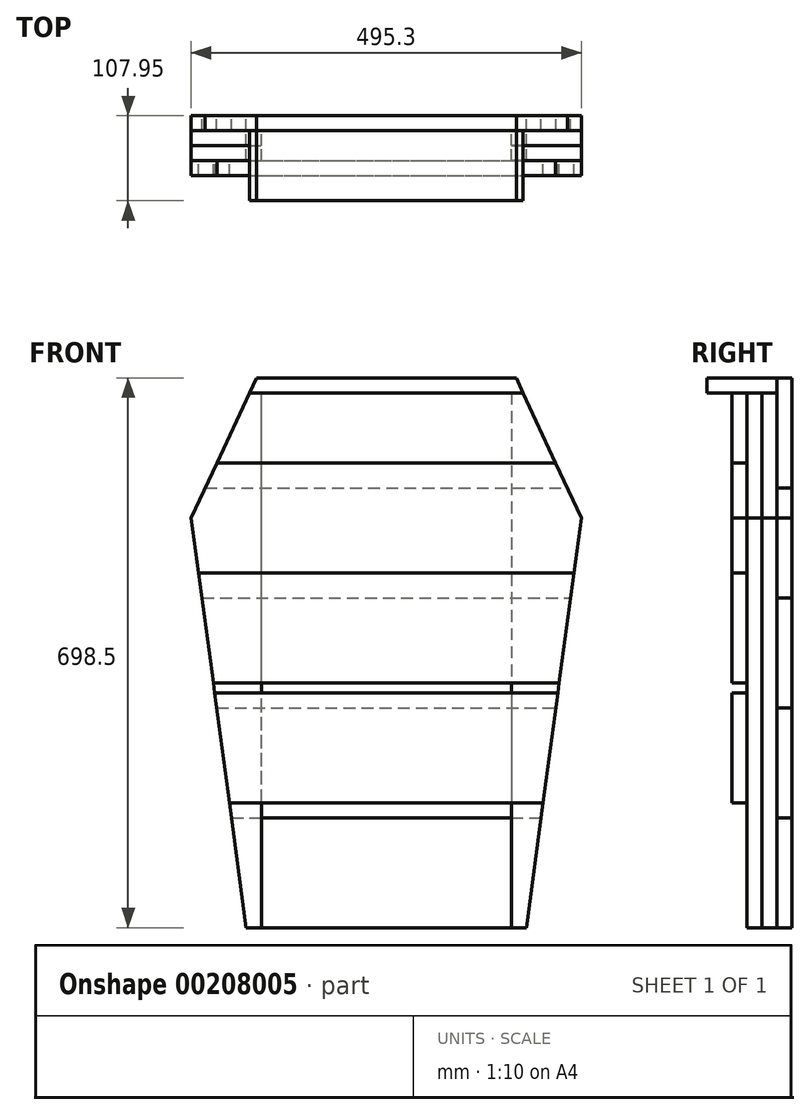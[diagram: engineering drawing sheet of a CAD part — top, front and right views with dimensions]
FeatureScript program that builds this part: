
annotation { "Feature Type Name" : "Feature", "Feature Type Description" : "" }
export const myFeature = defineFeature(function(context is Context, id is Id, definition is map)
    precondition{}
    {
        {
            var Q0;
            Q0=qCreatedBy(makeId("Front.planeOp"),FACE);
            var sketch = newSketch(context, id + "F0", { "sketchPlane" : qUnion([Q0])});
            skLineSegment(sketch, "E0", {"start": v(0, 0) * mm, "end": v(0, -698.5) * mm, "construction": true});
            skLineSegment(sketch, "E1", {"start": v(-165.1, 0) * mm, "end": v(165.1, 0) * mm});
            skLineSegment(sketch, "E2", {"start": v(165.1, 0) * mm, "end": v(247.65, -177.8) * mm});
            skLineSegment(sketch, "E3", {"start": v(247.65, -177.8) * mm, "end": v(177.8, -698.5) * mm});
            skLineSegment(sketch, "E4", {"start": v(177.8, -698.5) * mm, "end": v(-177.8, -698.5) * mm});
            skLineSegment(sketch, "E5", {"start": v(-177.8, -698.5) * mm, "end": v(-247.65, -177.8) * mm});
            skLineSegment(sketch, "E6", {"start": v(-247.65, -177.8) * mm, "end": v(-165.1, 0) * mm});
            skSolve(sketch);
        }
        {
            var Q0;
            Q0=qCreatedBy(makeId("Front.planeOp"),FACE);
            var sketch = newSketch(context, id + "F1", { "sketchPlane" : qUnion([Q0])});
            skLineSegment(sketch, "E7.0", {"start": v(-177.8, -698.5) * mm, "end": v(-247.65, -177.8) * mm});
            skLineSegment(sketch, "E8.0", {"start": v(-247.65, -177.8) * mm, "end": v(-165.1, 0) * mm});
            skLineSegment(sketch, "E8.1", {"start": v(-165.1, 0) * mm, "end": v(165.1, 0) * mm});
            skLineSegment(sketch, "E8.2", {"start": v(165.1, 0) * mm, "end": v(247.65, -177.8) * mm});
            skLineSegment(sketch, "E8.3", {"start": v(247.65, -177.8) * mm, "end": v(177.8, -698.5) * mm});
            skLineSegment(sketch, "E9", {"start": v(-229.96, -139.7) * mm, "end": v(229.96, -139.7) * mm});
            skLineSegment(sketch, "E10", {"start": v(-234.02, -279.4) * mm, "end": v(234.02, -279.4) * mm});
            skLineSegment(sketch, "E11", {"start": v(-215.28, -419.1) * mm, "end": v(215.28, -419.1) * mm});
            skLineSegment(sketch, "E12", {"start": v(-196.54, -558.8) * mm, "end": v(196.54, -558.8) * mm});
            skLineSegment(sketch, "E13", {"start": v(-177.8, -698.5) * mm, "end": v(177.8, -698.5) * mm});
            skSolve(sketch);
        }
        {
            var Q0;
            {var subQ0=sQuery(id+"F1.wireOp",EDGE,"E11");Q0=makeQuery(id+"F1.imprint","IMPRINT",FACE,{"disambiguationData":[TD([[makeQuery(id+"F1.imprint","IMPRINT",EDGE,{"derivedFrom":subQ0}),-1.0]])]});}
            var Q1;
            {var subQ7=sQuery(id+"F1.wireOp",EDGE,"E9");Q1=makeQuery(id+"F1.imprint","IMPRINT",FACE,{"disambiguationData":[TD([[makeQuery(id+"F1.imprint","IMPRINT",EDGE,{"derivedFrom":subQ7}),-1.0]])]});}
            extrude(context, id + "F2", {"entities" : qUnion([Q0, Q1]), "depth" : 19.05 * mm});
        }
        {
            var Q0;
            {var subQ0=sQuery(id+"F1.wireOp",EDGE,"E12");Q0=makeQuery(id+"F1.imprint","IMPRINT",FACE,{"disambiguationData":[TD([[makeQuery(id+"F1.imprint","IMPRINT",EDGE,{"derivedFrom":subQ0}),-1.0]])]});}
            var Q1;
            {var subQ0=sQuery(id+"F1.wireOp",EDGE,"E10");Q1=makeQuery(id+"F1.imprint","IMPRINT",FACE,{"disambiguationData":[TD([[makeQuery(id+"F1.imprint","IMPRINT",EDGE,{"derivedFrom":subQ0}),-1.0]])]});}
            var Q2;
            {var subQ0=sQuery(id+"F1.wireOp",EDGE,"E8.1");Q2=makeQuery(id+"F1.imprint","IMPRINT",FACE,{"disambiguationData":[TD([[makeQuery(id+"F1.imprint","IMPRINT",EDGE,{"derivedFrom":subQ0}),-1.0]])]});}
            extrude(context, id + "F3", {"entities" : qUnion([Q0, Q1, Q2]), "depth" : 19.05 * mm});
        }
        {
            var Q0;
            Q0=makeQuery(id+"F3.opExtrude","CAP_FACE",FACE,{"disambiguationData":[OSD([sQuery(id+"F1.wireOp",EDGE,"E8.0"),sQuery(id+"F1.wireOp",EDGE,"E8.1"),sQuery(id+"F1.wireOp",EDGE,"E8.2"),sQuery(id+"F1.wireOp",EDGE,"E9")])],"isStart":false});
            var sketch = newSketch(context, id + "F4", { "sketchPlane" : qUnion([Q0])});
            skLineSegment(sketch, "E14.0", {"start": v(-177.8, -698.5) * mm, "end": v(-247.65, -177.8) * mm});
            skLineSegment(sketch, "E14.1", {"start": v(-247.65, -177.8) * mm, "end": v(-165.1, 0) * mm});
            skLineSegment(sketch, "E14.3", {"start": v(165.1, 0) * mm, "end": v(247.65, -177.8) * mm});
            skLineSegment(sketch, "E14.4", {"start": v(247.65, -177.8) * mm, "end": v(177.8, -698.5) * mm});
            skLineSegment(sketch, "E14.9", {"start": v(-177.8, -698.5) * mm, "end": v(-158.75, -698.5) * mm});
            skLineSegment(sketch, "E15.0", {"start": v(-173.94, -19.05) * mm, "end": v(173.94, -19.05) * mm});
            skLineSegment(sketch, "E16.trimOffspring", {"start": v(158.75, -698.5) * mm, "end": v(177.8, -698.5) * mm});
            skLineSegment(sketch, "E17", {"start": v(-165.1, 0) * mm, "end": v(165.1, 0) * mm});
            skPoint(sketch, "E18.orphan", {"position": v(-165.1, 0) * mm});
            skPoint(sketch, "E19.orphan", {"position": v(165.1, 0) * mm});
            skLineSegment(sketch, "E20", {"start": v(-158.75, -698.5) * mm, "end": v(-158.75, -19.05) * mm});
            skLineSegment(sketch, "E21", {"start": v(158.75, -698.5) * mm, "end": v(158.75, -19.05) * mm});
            skSolve(sketch);
        }
        {
            var Q0;
            {var subQ0=sQuery(id+"F4.wireOp",EDGE,"E14.1");var subQ1=makeQuery(id+"F3.opExtrude","CAP_EDGE",EDGE,{"disambiguationData":[OSD([sQuery(id+"F1.wireOp",EDGE,"E9")])],"isStart":false});var subQ2=makeQuery(id+"F4.imprint","INTERSECT",VERTEX,{"derivedFrom":[subQ1,subQ0]});Q0=makeQuery(id+"F4.imprint","IMPRINT",FACE,{"disambiguationData":[TD([[makeQuery(id+"F4.imprint","IMPRINT",EDGE,{"disambiguationData":[TD([[subQ2,-1.0]])],"derivedFrom":subQ0}),-1.0]])]});}
            var Q1;
            {var subQ3=sQuery(id+"F4.wireOp",EDGE,"E14.0");Q1=makeQuery(id+"F4.imprint","IMPRINT",FACE,{"disambiguationData":[TD([[makeQuery(id+"F4.imprint","IMPRINT",EDGE,{"derivedFrom":subQ3}),-1.0]])]});}
            var Q2;
            {var subQ0=sQuery(id+"F4.wireOp",EDGE,"E14.3");var subQ1=makeQuery(id+"F3.opExtrude","CAP_EDGE",EDGE,{"disambiguationData":[OSD([sQuery(id+"F1.wireOp",EDGE,"E9")])],"isStart":false});var subQ2=makeQuery(id+"F4.imprint","INTERSECT",VERTEX,{"derivedFrom":[subQ1,subQ0]});Q2=makeQuery(id+"F4.imprint","IMPRINT",FACE,{"disambiguationData":[TD([[makeQuery(id+"F4.imprint","IMPRINT",EDGE,{"disambiguationData":[TD([[subQ2,1.0]])],"derivedFrom":subQ0}),-1.0]])]});}
            var Q3;
            {var subQ0=sQuery(id+"F4.wireOp",EDGE,"E14.4");Q3=makeQuery(id+"F4.imprint","IMPRINT",FACE,{"disambiguationData":[TD([[makeQuery(id+"F4.imprint","IMPRINT",EDGE,{"derivedFrom":subQ0}),-1.0]])]});}
            extrude(context, id + "F5", {"entities" : qUnion([Q0, Q1, Q2, Q3]), "depth" : 19.05 * mm});
        }
        {
            var Q0;
            Q0=makeQuery(id+"F5.opExtrude","CAP_FACE",FACE,{"disambiguationData":[OSD([sQuery(id+"F4.wireOp",EDGE,"E14.0"),sQuery(id+"F4.wireOp",EDGE,"E14.1"),sQuery(id+"F4.wireOp",EDGE,"E14.9"),sQuery(id+"F4.wireOp",EDGE,"E15.0"),sQuery(id+"F4.wireOp",EDGE,"E20")])],"isStart":false});
            var sketch = newSketch(context, id + "F6", { "sketchPlane" : qUnion([Q0])});
            skLineSegment(sketch, "E22.0.0", {"start": v(-177.8, -698.5) * mm, "end": v(-158.75, -698.5) * mm});
            skLineSegment(sketch, "E22.0.1", {"start": v(-158.75, -698.5) * mm, "end": v(-158.75, -19.05) * mm});
            skLineSegment(sketch, "E22.0.2", {"start": v(-158.75, -19.05) * mm, "end": v(-173.94, -19.05) * mm});
            skLineSegment(sketch, "E22.0.3", {"start": v(-173.94, -19.05) * mm, "end": v(-247.65, -177.8) * mm});
            skLineSegment(sketch, "E22.0.4", {"start": v(-247.65, -177.8) * mm, "end": v(-177.8, -698.5) * mm});
            skLineSegment(sketch, "E23.0.0", {"start": v(158.75, -19.05) * mm, "end": v(158.75, -698.5) * mm});
            skLineSegment(sketch, "E23.0.1", {"start": v(158.75, -698.5) * mm, "end": v(177.8, -698.5) * mm});
            skLineSegment(sketch, "E23.0.2", {"start": v(177.8, -698.5) * mm, "end": v(247.65, -177.8) * mm});
            skLineSegment(sketch, "E23.0.3", {"start": v(247.65, -177.8) * mm, "end": v(173.94, -19.05) * mm});
            skLineSegment(sketch, "E23.0.4", {"start": v(173.94, -19.05) * mm, "end": v(158.75, -19.05) * mm});
            skSolve(sketch);
        }
        {
            var Q0;
            Q0 = qSketchRegion(id + "F6", true);
            extrude(context, id + "F7", {"entities" : qUnion([Q0]), "depth" : 19.05 * mm});
        }
        {
            var Q0;
            {var subQ4=sQuery(id+"F4.wireOp",EDGE,"E17");Q0=makeQuery(id+"F4.imprint","IMPRINT",FACE,{"disambiguationData":[TD([[makeQuery(id+"F4.imprint","IMPRINT",EDGE,{"derivedFrom":subQ4}),-1.0]])]});}
            extrude(context, id + "F8", {"entities" : qUnion([Q0]), "depth" : 88.9 * mm});
        }
        {
            var Q0;
            Q0=makeQuery(id+"F7.opExtrude","CAP_FACE",FACE,{"disambiguationData":[OSD([sQuery(id+"F6.wireOp",EDGE,"E23.0.0"),sQuery(id+"F6.wireOp",EDGE,"E23.0.1"),sQuery(id+"F6.wireOp",EDGE,"E23.0.2"),sQuery(id+"F6.wireOp",EDGE,"E23.0.3"),sQuery(id+"F6.wireOp",EDGE,"E23.0.4")])],"isStart":false});
            var sketch = newSketch(context, id + "F9", { "sketchPlane" : qUnion([Q0])});
            skLineSegment(sketch, "E24.0", {"start": v(-173.94, -19.05) * mm, "end": v(173.94, -19.05) * mm});
            skLineSegment(sketch, "E25", {"start": v(-238.28, -247.65) * mm, "end": v(238.28, -247.65) * mm});
            skLineSegment(sketch, "E26", {"start": v(-219.54, -387.35) * mm, "end": v(219.54, -387.35) * mm});
            skLineSegment(sketch, "E27", {"start": v(-217.84, -400.05) * mm, "end": v(217.84, -400.05) * mm});
            skLineSegment(sketch, "E28", {"start": v(-199.1, -539.75) * mm, "end": v(199.1, -539.75) * mm});
            skLineSegment(sketch, "E29.1", {"start": v(-177.8, -698.5) * mm, "end": v(-247.65, -177.8) * mm});
            skLineSegment(sketch, "E29.3", {"start": v(247.65, -177.8) * mm, "end": v(177.8, -698.5) * mm});
            skLineSegment(sketch, "E30.0", {"start": v(247.65, -177.8) * mm, "end": v(173.94, -19.05) * mm});
            skLineSegment(sketch, "E31.0", {"start": v(-247.65, -177.8) * mm, "end": v(-173.94, -19.05) * mm});
            skLineSegment(sketch, "E32", {"start": v(-215.22, -107.95) * mm, "end": v(215.22, -107.95) * mm});
            skSolve(sketch);
        }
        {
            var Q0;
            {var subQ1=sQuery(id+"F9.wireOp",EDGE,"E25");Q0=makeQuery(id+"F9.imprint","IMPRINT",FACE,{"disambiguationData":[TD([[makeQuery(id+"F9.imprint","IMPRINT",EDGE,{"derivedFrom":subQ1}),1.0]])]});}
            var Q1;
            {var subQ0=sQuery(id+"F9.wireOp",EDGE,"E27");Q1=makeQuery(id+"F9.imprint","IMPRINT",FACE,{"disambiguationData":[TD([[makeQuery(id+"F9.imprint","IMPRINT",EDGE,{"derivedFrom":subQ0}),-1.0]])]});}
            var Q2;
            {var subQ0=sQuery(id+"F9.wireOp",EDGE,"E29.2");Q2=makeQuery(id+"F9.imprint","IMPRINT",FACE,{"disambiguationData":[TD([[makeQuery(id+"F9.imprint","IMPRINT",EDGE,{"derivedFrom":subQ0}),-1.0]])]});}
            extrude(context, id + "F10", {"entities" : qUnion([Q0, Q1, Q2]), "depth" : 19.05 * mm});
        }
        {
            var Q0;
            {var subQ0=sQuery(id+"F9.wireOp",EDGE,"E25");Q0=makeQuery(id+"F9.imprint","IMPRINT",FACE,{"disambiguationData":[TD([[makeQuery(id+"F9.imprint","IMPRINT",EDGE,{"derivedFrom":subQ0}),-1.0]])]});}
            var Q1;
            {var subQ0=sQuery(id+"F9.wireOp",EDGE,"E24.0");var subQ3=sQuery(id+"F9.wireOp",EDGE,"E31.0");var subQ4=makeQuery(id+"F9.imprint","INTERSECT",VERTEX,{"derivedFrom":[subQ0,subQ3]});Q1=makeQuery(id+"F9.imprint","IMPRINT",FACE,{"disambiguationData":[TD([[makeQuery(id+"F9.imprint","IMPRINT",EDGE,{"disambiguationData":[TD([[subQ4,-1.0]])],"derivedFrom":subQ0}),-1.0]])]});}
            var Q2;
            {var subQ0=sQuery(id+"F9.wireOp",EDGE,"E24.0");var subQ3=sQuery(id+"F9.wireOp",EDGE,"E30.0");var subQ4=makeQuery(id+"F9.imprint","INTERSECT",VERTEX,{"derivedFrom":[subQ0,subQ3]});Q2=makeQuery(id+"F9.imprint","IMPRINT",FACE,{"disambiguationData":[TD([[makeQuery(id+"F9.imprint","IMPRINT",EDGE,{"disambiguationData":[TD([[subQ4,-1.0]])],"derivedFrom":subQ0}),1.0]])]});}
            extrude(context, id + "F11", {"entities" : qUnion([Q0, Q1, Q2]), "depth" : 19.05 * mm});
        }
    });
